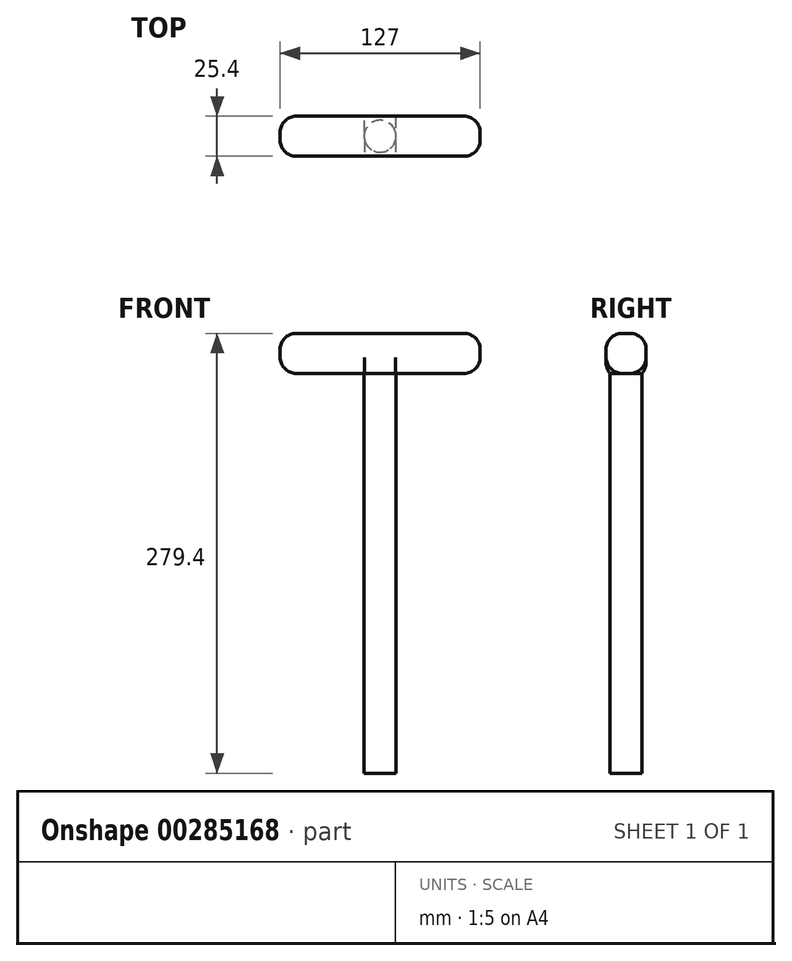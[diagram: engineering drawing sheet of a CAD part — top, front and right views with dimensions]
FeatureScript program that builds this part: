
annotation { "Feature Type Name" : "Feature", "Feature Type Description" : "" }
export const myFeature = defineFeature(function(context is Context, id is Id, definition is map)
    precondition{}
    {
        {
            var Q0;
            Q0=qCreatedBy(makeId("Front.planeOp"),FACE);
            var sketch = newSketch(context, id + "F0", { "sketchPlane" : qUnion([Q0])});
            skLineSegment(sketch, "E0.bottom", {"start": v(0, 0) * mm, "end": v(-127, 0) * mm});
            skLineSegment(sketch, "E0.top", {"start": v(0, 25.4) * mm, "end": v(-127, 25.4) * mm});
            skLineSegment(sketch, "E0.left", {"start": v(0, 0) * mm, "end": v(0, 25.4) * mm});
            skLineSegment(sketch, "E0.right", {"start": v(-127, 0) * mm, "end": v(-127, 25.4) * mm});
            skSolve(sketch);
        }
        {
            var Q0;
            Q0=makeQuery(id+"F0.imprint","IMPRINT",FACE,{"disambiguationData":[TD([[makeQuery(id+"F0.imprint","IMPRINT",EDGE,{"derivedFrom":sQuery(id+"F0.wireOp",EDGE,"E0.bottom")}),-1.0]])]});
            extrude(context, id + "F1", {"entities" : qUnion([Q0]), "depth" : 25.4 * mm});
        }
        {
            var Q0;
            Q0=makeQuery(id+"F1.opExtrude","SWEPT_FACE",FACE,{"disambiguationData":[OSD([sQuery(id+"F0.wireOp",EDGE,"E0.bottom")])]});
            var sketch = newSketch(context, id + "F2", { "sketchPlane" : qUnion([Q0])});
            skLineSegment(sketch, "E1", {"start": v(-127, 12.7) * mm, "end": v(0, 12.7) * mm, "construction": true});
            skCircle(sketch, "E2", {"center": v(-63.5, 12.7) * mm, "radius": 10.16 * mm});
            skSolve(sketch);
        }
        {
            var Q0;
            Q0=makeQuery(id+"F2.imprint","IMPRINT",FACE,{"disambiguationData":[TD([[makeQuery(id+"F2.imprint","IMPRINT",EDGE,{"derivedFrom":sQuery(id+"F2.wireOp",EDGE,"E2")}),1.0]])]});
            extrude(context, id + "F3", {"entities" : qUnion([Q0]), "operationType" : NewBodyOperationType.ADD, "depth" : 254 * mm});
        }
        {
            var Q0;
            Q0=makeQuery(id+"F1.opExtrude","CAP_EDGE",EDGE,{"disambiguationData":[OSD([sQuery(id+"F0.wireOp",EDGE,"E0.right")])],"isStart":false});
            var Q1;
            Q1=makeQuery(id+"F1.opExtrude","CAP_EDGE",EDGE,{"disambiguationData":[OSD([sQuery(id+"F0.wireOp",EDGE,"E0.left")])],"isStart":false});
            var Q2;
            Q2=makeQuery(id+"F1.opExtrude","SWEPT_EDGE",EDGE,{"disambiguationData":[OSD([sQuery(id+"F0.wireOp",EDGE,"E0.top"),sQuery(id+"F0.wireOp",EDGE,"E0.left")])]});
            var Q3;
            Q3=makeQuery(id+"F1.opExtrude","SWEPT_FACE",FACE,{"disambiguationData":[OSD([sQuery(id+"F0.wireOp",EDGE,"E0.left")])]});
            var Q4;
            Q4=makeQuery(id+"F1.opExtrude","SWEPT_EDGE",EDGE,{"disambiguationData":[OSD([sQuery(id+"F0.wireOp",EDGE,"E0.bottom"),sQuery(id+"F0.wireOp",EDGE,"E0.left")])]});
            var Q5;
            Q5=makeQuery(id+"F1.opExtrude","CAP_EDGE",EDGE,{"disambiguationData":[OSD([sQuery(id+"F0.wireOp",EDGE,"E0.top")])],"isStart":false});
            var Q6;
            Q6=makeQuery(id+"F1.opExtrude","CAP_EDGE",EDGE,{"disambiguationData":[OSD([sQuery(id+"F0.wireOp",EDGE,"E0.bottom")])],"isStart":false});
            var Q7;
            Q7=makeQuery(id+"F1.opExtrude","SWEPT_EDGE",EDGE,{"disambiguationData":[OSD([sQuery(id+"F0.wireOp",EDGE,"E0.top"),sQuery(id+"F0.wireOp",EDGE,"E0.right")])]});
            var Q8;
            Q8=makeQuery(id+"F1.opExtrude","CAP_EDGE",EDGE,{"disambiguationData":[OSD([sQuery(id+"F0.wireOp",EDGE,"E0.top")])],"isStart":true});
            var Q9;
            Q9=makeQuery(id+"F1.opExtrude","CAP_EDGE",EDGE,{"disambiguationData":[OSD([sQuery(id+"F0.wireOp",EDGE,"E0.bottom")])],"isStart":true});
            var Q10;
            Q10=makeQuery(id+"F1.opExtrude","CAP_EDGE",EDGE,{"disambiguationData":[OSD([sQuery(id+"F0.wireOp",EDGE,"E0.right")])],"isStart":true});
            var Q11;
            Q11=makeQuery(id+"F1.opExtrude","SWEPT_EDGE",EDGE,{"disambiguationData":[OSD([sQuery(id+"F0.wireOp",EDGE,"E0.bottom"),sQuery(id+"F0.wireOp",EDGE,"E0.right")])]});
            fillet(context, id + "F4", {"entities" : qUnion([Q0, Q1, Q2, Q3, Q4, Q5, Q6, Q7, Q8, Q9, Q10, Q11]), "radius" : 10.16 * mm, "tangentPropagation" : true, "allowEdgeOverflow" : false});
        }
    });
